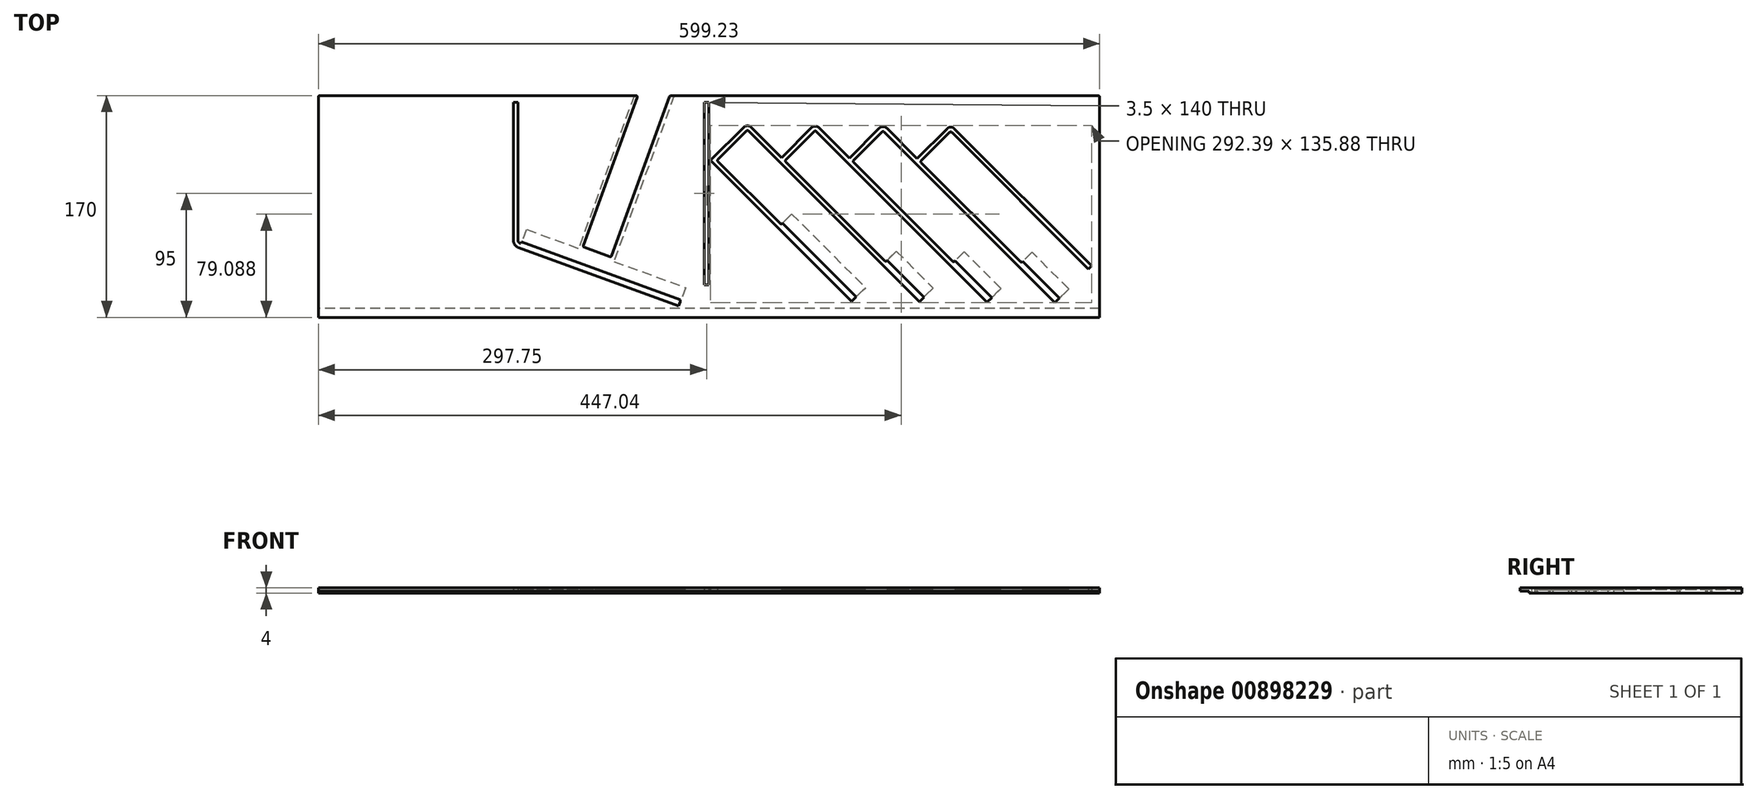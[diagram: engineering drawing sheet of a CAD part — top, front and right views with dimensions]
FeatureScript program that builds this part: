
annotation { "Feature Type Name" : "Feature", "Feature Type Description" : "" }
export const myFeature = defineFeature(function(context is Context, id is Id, definition is map)
    precondition{}
    {
        {
            var Q0;
            Q0=qCreatedBy(makeId("Top.planeOp"),FACE);
            var sketch = newSketch(context, id + "F0", { "sketchPlane" : qUnion([Q0])});
            skLineSegment(sketch, "E0.left", {"start": v(299.43, -88.5) * mm, "end": v(299.43, 80.5) * mm});
            skLineSegment(sketch, "E0.right", {"start": v(-299.8, -88.5) * mm, "end": v(-299.8, 80.5) * mm});
            skPoint(sketch, "E0.middle", {"position": v(0, 0) * mm});
            skLineSegment(sketch, "E1", {"start": v(188.08, 56.3) * mm, "end": v(293.43, -49.07) * mm});
            skLineSegment(sketch, "E2", {"start": v(293.43, -49.07) * mm, "end": v(290.96, -51.54) * mm});
            skLineSegment(sketch, "E3", {"start": v(265.15, -77.35) * mm, "end": v(156.96, 30.84) * mm});
            skLineSegment(sketch, "E4", {"start": v(159.44, 33.31) * mm, "end": v(182.42, 56.3) * mm});
            skLineSegment(sketch, "E5", {"start": v(238.63, -45.88) * mm, "end": v(162.62, 30.13) * mm});
            skLineSegment(sketch, "E6", {"start": v(162.62, 31.54) * mm, "end": v(184.54, 53.46) * mm});
            skLineSegment(sketch, "E7", {"start": v(185.95, 53.46) * mm, "end": v(290.96, -51.54) * mm});
            skLineSegment(sketch, "E8.trimOffspring", {"start": v(267.62, -74.88) * mm, "end": v(265.15, -77.35) * mm});
            skLineSegment(sketch, "E9", {"start": v(136.1, 56.65) * mm, "end": v(159.44, 33.31) * mm});
            skLineSegment(sketch, "E10", {"start": v(213.18, -77) * mm, "end": v(105, 31.2) * mm});
            skLineSegment(sketch, "E11", {"start": v(107.47, 33.67) * mm, "end": v(130.45, 56.65) * mm});
            skLineSegment(sketch, "E12", {"start": v(186.66, -45.53) * mm, "end": v(110.65, 30.48) * mm});
            skLineSegment(sketch, "E13", {"start": v(110.65, 31.9) * mm, "end": v(132.57, 53.82) * mm});
            skLineSegment(sketch, "E14", {"start": v(133.98, 53.82) * mm, "end": v(156.96, 30.84) * mm});
            skLineSegment(sketch, "E15.trimOffspring", {"start": v(215.65, -74.52) * mm, "end": v(213.18, -77) * mm});
            skLineSegment(sketch, "E16", {"start": v(84.13, 57) * mm, "end": v(107.47, 33.67) * mm});
            skLineSegment(sketch, "E17", {"start": v(161.2, -76.64) * mm, "end": v(53.02, 31.54) * mm});
            skLineSegment(sketch, "E18", {"start": v(55.5, 34.02) * mm, "end": v(78.47, 57) * mm});
            skLineSegment(sketch, "E19", {"start": v(134.69, -45.18) * mm, "end": v(58.67, 30.84) * mm});
            skLineSegment(sketch, "E20", {"start": v(58.67, 32.25) * mm, "end": v(80.6, 54.17) * mm});
            skLineSegment(sketch, "E21", {"start": v(82, 54.17) * mm, "end": v(105, 31.2) * mm});
            skLineSegment(sketch, "E22.trimOffspring", {"start": v(163.68, -74.17) * mm, "end": v(161.2, -76.64) * mm});
            skLineSegment(sketch, "E23", {"start": v(32.16, 57.35) * mm, "end": v(55.5, 34.02) * mm});
            skLineSegment(sketch, "E24", {"start": v(109.23, -76.29) * mm, "end": v(1.05, 31.9) * mm});
            skLineSegment(sketch, "E25", {"start": v(1.05, 31.9) * mm, "end": v(26.5, 57.35) * mm});
            skLineSegment(sketch, "E26", {"start": v(54.43, -16.54) * mm, "end": v(6.7, 31.2) * mm});
            skLineSegment(sketch, "E27", {"start": v(6.7, 32.6) * mm, "end": v(28.62, 54.53) * mm});
            skLineSegment(sketch, "E28", {"start": v(30.04, 54.53) * mm, "end": v(53.02, 31.54) * mm});
            skLineSegment(sketch, "E29.trimOffspring", {"start": v(111.7, -73.81) * mm, "end": v(109.23, -76.29) * mm});
            skLineSegment(sketch, "E30", {"start": v(-3.8, 76.5) * mm, "end": v(-3.8, -63.5) * mm});
            skLineSegment(sketch, "E31", {"start": v(-3.8, -63.5) * mm, "end": v(-0.3, -63.5) * mm});
            skLineSegment(sketch, "E32", {"start": v(-0.3, -63.5) * mm, "end": v(-0.3, 76.5) * mm});
            skLineSegment(sketch, "E33", {"start": v(-0.3, 76.5) * mm, "end": v(-3.8, 76.5) * mm});
            skLineSegment(sketch, "E34", {"start": v(-299.8, -88.5) * mm, "end": v(299.43, -88.5) * mm});
            skLineSegment(sketch, "E35", {"start": v(-150.3, 76.5) * mm, "end": v(-150.3, -29.3) * mm});
            skLineSegment(sketch, "E36", {"start": v(-146.36, -34.93) * mm, "end": v(-23.49, -79.8) * mm});
            skLineSegment(sketch, "E37", {"start": v(-23.49, -79.8) * mm, "end": v(-22.29, -76.5) * mm});
            skLineSegment(sketch, "E38", {"start": v(-146.8, -29.09) * mm, "end": v(-146.8, 76.5) * mm});
            skPoint(sketch, "E39.orphan", {"position": v(-299.8, -121.5) * mm});
            skPoint(sketch, "E40.orphan", {"position": v(299.43, -122.07) * mm});
            skPoint(sketch, "E41.visualSharp", {"position": v(-146.8, -31.19) * mm});
            skArc(sketch, "E41.filletArc", {"start": v(-146.8, -29.09) * mm, "mid": v(-146.26, -30.8) * mm, "end": v(-144.83, -31.9) * mm});
            skPoint(sketch, "E42.visualSharp", {"position": v(-150.3, -33.5) * mm});
            skArc(sketch, "E42.filletArc", {"start": v(-150.3, -29.3) * mm, "mid": v(-149.22, -32.74) * mm, "end": v(-146.36, -34.93) * mm});
            skLineSegment(sketch, "E43", {"start": v(267.62, -74.88) * mm, "end": v(268.69, -73.81) * mm});
            skLineSegment(sketch, "E44", {"start": v(268.69, -73.81) * mm, "end": v(240.4, -45.53) * mm});
            skLineSegment(sketch, "E45", {"start": v(240.4, -45.53) * mm, "end": v(240.05, -45.88) * mm});
            skLineSegment(sketch, "E46", {"start": v(215.65, -74.52) * mm, "end": v(216.71, -73.46) * mm});
            skLineSegment(sketch, "E47", {"start": v(216.71, -73.46) * mm, "end": v(188.43, -45.18) * mm});
            skLineSegment(sketch, "E48", {"start": v(188.43, -45.18) * mm, "end": v(188.08, -45.53) * mm});
            skLineSegment(sketch, "E49", {"start": v(163.68, -74.17) * mm, "end": v(164.74, -73.1) * mm});
            skLineSegment(sketch, "E50", {"start": v(164.74, -73.1) * mm, "end": v(136.46, -44.82) * mm});
            skLineSegment(sketch, "E51", {"start": v(136.46, -44.82) * mm, "end": v(136.1, -45.18) * mm});
            skLineSegment(sketch, "E52", {"start": v(111.7, -73.81) * mm, "end": v(112.77, -72.75) * mm});
            skLineSegment(sketch, "E53", {"start": v(112.77, -72.75) * mm, "end": v(56.2, -16.19) * mm});
            skLineSegment(sketch, "E54", {"start": v(56.2, -16.19) * mm, "end": v(55.85, -16.54) * mm});
            skLineSegment(sketch, "E55", {"start": v(-144.83, -31.9) * mm, "end": v(-144.31, -30.5) * mm});
            skLineSegment(sketch, "E56", {"start": v(-144.31, -30.5) * mm, "end": v(-101.09, -46.23) * mm});
            skPoint(sketch, "E57.visualSharp", {"position": v(29.33, 60.18) * mm});
            skArc(sketch, "E57.filletArc", {"start": v(32.16, 57.35) * mm, "mid": v(29.33, 58.53) * mm, "end": v(26.5, 57.35) * mm});
            skPoint(sketch, "E58.visualSharp", {"position": v(81.3, 59.83) * mm});
            skArc(sketch, "E58.filletArc", {"start": v(84.13, 57) * mm, "mid": v(81.3, 58.17) * mm, "end": v(78.47, 57) * mm});
            skPoint(sketch, "E59.visualSharp", {"position": v(133.27, 59.48) * mm});
            skArc(sketch, "E59.filletArc", {"start": v(136.1, 56.65) * mm, "mid": v(133.27, 57.82) * mm, "end": v(130.45, 56.65) * mm});
            skPoint(sketch, "E60.visualSharp", {"position": v(185.25, 59.12) * mm});
            skArc(sketch, "E60.filletArc", {"start": v(188.08, 56.3) * mm, "mid": v(185.25, 57.46) * mm, "end": v(182.42, 56.3) * mm});
            skPoint(sketch, "E61.visualSharp", {"position": v(6, 31.9) * mm});
            skArc(sketch, "E61.filletArc", {"start": v(6.7, 32.6) * mm, "mid": v(6.4, 31.9) * mm, "end": v(6.7, 31.2) * mm});
            skPoint(sketch, "E62.visualSharp", {"position": v(57.97, 31.54) * mm});
            skArc(sketch, "E62.filletArc", {"start": v(58.67, 32.25) * mm, "mid": v(58.38, 31.54) * mm, "end": v(58.67, 30.84) * mm});
            skPoint(sketch, "E63.visualSharp", {"position": v(109.94, 31.2) * mm});
            skArc(sketch, "E63.filletArc", {"start": v(110.65, 31.9) * mm, "mid": v(110.35, 31.2) * mm, "end": v(110.65, 30.48) * mm});
            skPoint(sketch, "E64.visualSharp", {"position": v(161.91, 30.84) * mm});
            skArc(sketch, "E64.filletArc", {"start": v(162.62, 31.54) * mm, "mid": v(162.33, 30.84) * mm, "end": v(162.62, 30.13) * mm});
            skPoint(sketch, "E65.visualSharp", {"position": v(81.3, 54.88) * mm});
            skArc(sketch, "E65.filletArc", {"start": v(82, 54.17) * mm, "mid": v(81.3, 54.46) * mm, "end": v(80.6, 54.17) * mm});
            skPoint(sketch, "E66.visualSharp", {"position": v(29.33, 55.23) * mm});
            skArc(sketch, "E66.filletArc", {"start": v(30.04, 54.53) * mm, "mid": v(29.33, 54.82) * mm, "end": v(28.62, 54.53) * mm});
            skPoint(sketch, "E67.visualSharp", {"position": v(133.27, 54.53) * mm});
            skArc(sketch, "E67.filletArc", {"start": v(133.98, 53.82) * mm, "mid": v(133.27, 54.11) * mm, "end": v(132.57, 53.82) * mm});
            skPoint(sketch, "E68.visualSharp", {"position": v(185.25, 54.17) * mm});
            skArc(sketch, "E68.filletArc", {"start": v(185.95, 53.46) * mm, "mid": v(185.25, 53.76) * mm, "end": v(184.54, 53.46) * mm});
            skLineSegment(sketch, "E69", {"start": v(-96.58, -33.5) * mm, "end": v(-55.2, 80.16) * mm});
            skLineSegment(sketch, "E70", {"start": v(-32.58, 75.09) * mm, "end": v(-74.96, -41.37) * mm});
            skLineSegment(sketch, "E71", {"start": v(-76.25, -41.97) * mm, "end": v(-95.98, -34.79) * mm});
            skLineSegment(sketch, "E72", {"start": v(-298.8, 81.5) * mm, "end": v(-202.52, 81.5) * mm});
            skLineSegment(sketch, "E73", {"start": v(-150.3, 76.5) * mm, "end": v(-146.8, 76.5) * mm});
            skLineSegment(sketch, "E74", {"start": v(-32.58, 75.09) * mm, "end": v(-30.48, 80.84) * mm});
            skLineSegment(sketch, "E75.trimOffspring", {"start": v(-175.92, 81.5) * mm, "end": v(-56.15, 81.5) * mm});
            skLineSegment(sketch, "E76.trimOffspring", {"start": v(-29.54, 81.5) * mm, "end": v(298.43, 81.5) * mm});
            skPoint(sketch, "E77.visualSharp", {"position": v(-299.8, 81.5) * mm});
            skArc(sketch, "E77.filletArc", {"start": v(-298.8, 81.5) * mm, "mid": v(-299.5, 81.2) * mm, "end": v(-299.8, 80.5) * mm});
            skPoint(sketch, "E78.visualSharp", {"position": v(299.43, 81.5) * mm});
            skArc(sketch, "E78.filletArc", {"start": v(299.43, 80.5) * mm, "mid": v(299.14, 81.2) * mm, "end": v(298.43, 81.5) * mm});
            skPoint(sketch, "E79.visualSharp", {"position": v(-30.24, 81.5) * mm});
            skArc(sketch, "E79.filletArc", {"start": v(-29.54, 81.5) * mm, "mid": v(-30.12, 81.32) * mm, "end": v(-30.48, 80.84) * mm});
            skPoint(sketch, "E80.visualSharp", {"position": v(-54.72, 81.5) * mm});
            skArc(sketch, "E80.filletArc", {"start": v(-55.2, 80.16) * mm, "mid": v(-55.33, 81.07) * mm, "end": v(-56.15, 81.5) * mm});
            skPoint(sketch, "E81.visualSharp", {"position": v(-101.6, -47.64) * mm});
            skLineSegment(sketch, "E82", {"start": v(-202.52, 81.5) * mm, "end": v(-175.92, 81.5) * mm});
            skLineSegment(sketch, "E83", {"start": v(-101.09, -46.23) * mm, "end": v(-69.14, -57.86) * mm});
            skPoint(sketch, "E84.visualSharp", {"position": v(-96.92, -34.45) * mm});
            skArc(sketch, "E84.filletArc", {"start": v(-96.58, -33.5) * mm, "mid": v(-96.54, -34.27) * mm, "end": v(-95.98, -34.79) * mm});
            skPoint(sketch, "E85.visualSharp", {"position": v(-75.3, -42.31) * mm});
            skArc(sketch, "E85.filletArc", {"start": v(-76.25, -41.97) * mm, "mid": v(-75.48, -41.94) * mm, "end": v(-74.96, -41.37) * mm});
            skPoint(sketch, "E86.visualSharp", {"position": v(-69.65, -59.27) * mm});
            skPoint(sketch, "E87.visualSharp", {"position": v(55.14, -17.25) * mm});
            skArc(sketch, "E87.filletArc", {"start": v(54.43, -16.54) * mm, "mid": v(55.14, -16.83) * mm, "end": v(55.85, -16.54) * mm});
            skPoint(sketch, "E88.visualSharp", {"position": v(135.4, -45.88) * mm});
            skArc(sketch, "E88.filletArc", {"start": v(134.69, -45.18) * mm, "mid": v(135.4, -45.47) * mm, "end": v(136.1, -45.18) * mm});
            skPoint(sketch, "E89.visualSharp", {"position": v(187.37, -46.24) * mm});
            skArc(sketch, "E89.filletArc", {"start": v(186.66, -45.53) * mm, "mid": v(187.37, -45.82) * mm, "end": v(188.08, -45.53) * mm});
            skPoint(sketch, "E90.visualSharp", {"position": v(239.34, -46.6) * mm});
            skArc(sketch, "E90.filletArc", {"start": v(238.63, -45.88) * mm, "mid": v(239.34, -46.18) * mm, "end": v(240.05, -45.88) * mm});
            skLineSegment(sketch, "E91", {"start": v(-69.14, -57.86) * mm, "end": v(-22.29, -74.91) * mm});
            skLineSegment(sketch, "E92", {"start": v(-22.29, -74.91) * mm, "end": v(-22.29, -76.5) * mm});
            skSolve(sketch);
        }
        {
            var Q0;
            Q0=qSketchRegion(id+"F0",true);
            extrude(context, id + "F1", {"entities" : qUnion([Q0]), "depth" : 4 * mm});
        }
        {
            var Q0;
            Q0=makeQuery(id+"F1.opExtrude","CAP_FACE",FACE,{"disambiguationData":[OSD([sQuery(id+"F0.wireOp",EDGE,"E0.top"),sQuery(id+"F0.wireOp",EDGE,"E0.left"),sQuery(id+"F0.wireOp",EDGE,"E0.right"),sQuery(id+"F0.wireOp",EDGE,"E1"),sQuery(id+"F0.wireOp",EDGE,"E2"),sQuery(id+"F0.wireOp",EDGE,"E3"),sQuery(id+"F0.wireOp",EDGE,"E4"),sQuery(id+"F0.wireOp",EDGE,"E5"),sQuery(id+"F0.wireOp",EDGE,"E6"),sQuery(id+"F0.wireOp",EDGE,"E7"),sQuery(id+"F0.wireOp",EDGE,"E8.trimOffspring"),sQuery(id+"F0.wireOp",EDGE,"E9"),sQuery(id+"F0.wireOp",EDGE,"E10"),sQuery(id+"F0.wireOp",EDGE,"E11"),sQuery(id+"F0.wireOp",EDGE,"E12"),sQuery(id+"F0.wireOp",EDGE,"E13"),sQuery(id+"F0.wireOp",EDGE,"E14"),sQuery(id+"F0.wireOp",EDGE,"E15.trimOffspring"),sQuery(id+"F0.wireOp",EDGE,"E16"),sQuery(id+"F0.wireOp",EDGE,"E17"),sQuery(id+"F0.wireOp",EDGE,"E18"),sQuery(id+"F0.wireOp",EDGE,"E19"),sQuery(id+"F0.wireOp",EDGE,"E20"),sQuery(id+"F0.wireOp",EDGE,"E21"),sQuery(id+"F0.wireOp",EDGE,"E22.trimOffspring"),sQuery(id+"F0.wireOp",EDGE,"E23"),sQuery(id+"F0.wireOp",EDGE,"E24"),sQuery(id+"F0.wireOp",EDGE,"E25"),sQuery(id+"F0.wireOp",EDGE,"E26"),sQuery(id+"F0.wireOp",EDGE,"E27"),sQuery(id+"F0.wireOp",EDGE,"E28"),sQuery(id+"F0.wireOp",EDGE,"E29.trimOffspring"),sQuery(id+"F0.wireOp",EDGE,"E30"),sQuery(id+"F0.wireOp",EDGE,"E31"),sQuery(id+"F0.wireOp",EDGE,"E32"),sQuery(id+"F0.wireOp",EDGE,"E33"),sQuery(id+"F0.wireOp",EDGE,"E34"),sQuery(id+"F0.wireOp",EDGE,"8IGRu6me-QNIK-KxZd-YoE2-obK5ITrom9I0"),sQuery(id+"F0.wireOp",EDGE,"ET2SPLNs-E16K-yzbb-k3nE-j9QhBZggRVGa"),sQuery(id+"F0.wireOp",EDGE,"ztZXadrO-MKuG-NGwv-NWga-JcB19pq0CV4f"),sQuery(id+"F0.wireOp",EDGE,"rMW3URec-0C8R-i97H-GSKa-9mzG0eoT4OPy"),sQuery(id+"F0.wireOp",EDGE,"l2nM3VSt-hcp3-IfvZ-Vc9z-1xBHJXzoDHYJ"),sQuery(id+"F0.wireOp",EDGE,"7f4JG1PR-e8fq-IrSw-QAHP-AJHShleLprlO"),sQuery(id+"F0.wireOp",EDGE,"E35"),sQuery(id+"F0.wireOp",EDGE,"E36"),sQuery(id+"F0.wireOp",EDGE,"E37"),sQuery(id+"F0.wireOp",EDGE,"Wq4ZA5YM-xzJ0-yVii-3j4H-AYTGBk09bdcb"),sQuery(id+"F0.wireOp",EDGE,"E38"),sQuery(id+"F0.wireOp",EDGE,"gIA7jmsT-nlDV-00d0-acZ5-NCJ1QFAXyANS")])],"isStart":true});
            var sketch = newSketch(context, id + "F2", { "sketchPlane" : qUnion([Q0])});
            skLineSegment(sketch, "E93", {"start": v(-299.8, 88.5) * mm, "end": v(299.43, 88.5) * mm});
            skLineSegment(sketch, "E94", {"start": v(299.43, 88.5) * mm, "end": v(299.43, 81.5) * mm});
            skLineSegment(sketch, "E95", {"start": v(299.43, 81.5) * mm, "end": v(-299.8, 81.5) * mm});
            skLineSegment(sketch, "E96", {"start": v(-299.8, 81.5) * mm, "end": v(-299.8, 88.5) * mm});
            skLineSegment(sketch, "E97", {"start": v(268.69, 73.81) * mm, "end": v(275.76, 66.74) * mm});
            skLineSegment(sketch, "E98", {"start": v(275.76, 66.74) * mm, "end": v(247.47, 38.46) * mm});
            skLineSegment(sketch, "E99", {"start": v(247.47, 38.46) * mm, "end": v(240.4, 45.53) * mm});
            skLineSegment(sketch, "E100", {"start": v(216.71, 73.46) * mm, "end": v(223.78, 66.39) * mm});
            skLineSegment(sketch, "E101", {"start": v(223.78, 66.39) * mm, "end": v(195.5, 38.1) * mm});
            skLineSegment(sketch, "E102", {"start": v(195.5, 38.1) * mm, "end": v(188.43, 45.18) * mm});
            skLineSegment(sketch, "E103", {"start": v(268.69, 73.81) * mm, "end": v(240.4, 45.53) * mm});
            skLineSegment(sketch, "E104", {"start": v(216.71, 73.46) * mm, "end": v(188.43, 45.18) * mm});
            skLineSegment(sketch, "E105", {"start": v(164.74, 73.1) * mm, "end": v(136.46, 44.82) * mm});
            skLineSegment(sketch, "E106", {"start": v(136.46, 44.82) * mm, "end": v(143.53, 37.75) * mm});
            skLineSegment(sketch, "E107", {"start": v(143.53, 37.75) * mm, "end": v(171.81, 66.04) * mm});
            skLineSegment(sketch, "E108", {"start": v(171.81, 66.04) * mm, "end": v(164.74, 73.1) * mm});
            skLineSegment(sketch, "E109", {"start": v(112.77, 72.75) * mm, "end": v(56.2, 16.19) * mm});
            skLineSegment(sketch, "E110", {"start": v(56.2, 16.19) * mm, "end": v(63.27, 9.11) * mm});
            skLineSegment(sketch, "E111", {"start": v(63.27, 9.11) * mm, "end": v(119.84, 65.68) * mm});
            skLineSegment(sketch, "E112", {"start": v(119.84, 65.68) * mm, "end": v(112.77, 72.75) * mm});
            skLineSegment(sketch, "E113", {"start": v(-1004.52, -17.26) * mm, "end": v(-1004.52, -17.26) * mm});
            skLineSegment(sketch, "E114", {"start": v(-52.4, -86.26) * mm, "end": v(-55.41, -87.35) * mm});
            skLineSegment(sketch, "E115", {"start": v(-55.41, -87.35) * mm, "end": v(-100.24, 35.8) * mm});
            skLineSegment(sketch, "E116", {"start": v(-100.24, 35.8) * mm, "end": v(-140.4, 21.19) * mm});
            skLineSegment(sketch, "E117", {"start": v(-140.4, 21.19) * mm, "end": v(-143.98, 31.05) * mm});
            skLineSegment(sketch, "E118", {"start": v(-28.6, -86.07) * mm, "end": v(-25.59, -84.97) * mm});
            skLineSegment(sketch, "E119", {"start": v(-25.59, -84.97) * mm, "end": v(-73.14, 45.67) * mm});
            skLineSegment(sketch, "E120", {"start": v(-52.4, -86.26) * mm, "end": v(-96, 33.37) * mm});
            skLineSegment(sketch, "E121", {"start": v(-96, 33.37) * mm, "end": v(-75.15, 41.3) * mm});
            skLineSegment(sketch, "E122", {"start": v(-143.98, 31.05) * mm, "end": v(-21.7, 75.56) * mm});
            skLineSegment(sketch, "E123", {"start": v(-73.14, 45.67) * mm, "end": v(-18.14, 65.68) * mm});
            skLineSegment(sketch, "E124", {"start": v(-18.14, 65.68) * mm, "end": v(-21.7, 75.56) * mm});
            skLineSegment(sketch, "E125", {"start": v(-75.15, 41.3) * mm, "end": v(-28.77, -86.14) * mm});
            skLineSegment(sketch, "E126", {"start": v(-28.77, -86.14) * mm, "end": v(-28.6, -86.07) * mm});
            skSolve(sketch);
        }
        {
            var Q0;
            Q0=makeQuery(id+"F2.imprint","IMPRINT",FACE,{"disambiguationData":[TD([[makeQuery(id+"F2.imprint","IMPRINT",EDGE,{"derivedFrom":sQuery(id+"F2.wireOp",EDGE,"E97")}),-1.0]])]});
            var Q1;
            Q1=makeQuery(id+"F2.imprint","IMPRINT",FACE,{"disambiguationData":[TD([[makeQuery(id+"F2.imprint","IMPRINT",EDGE,{"derivedFrom":sQuery(id+"F2.wireOp",EDGE,"E100")}),-1.0]])]});
            var Q2;
            Q2=makeQuery(id+"F2.imprint","IMPRINT",FACE,{"disambiguationData":[TD([[makeQuery(id+"F2.imprint","IMPRINT",EDGE,{"derivedFrom":sQuery(id+"F2.wireOp",EDGE,"E105")}),1.0]])]});
            var Q3;
            Q3=makeQuery(id+"F2.imprint","IMPRINT",FACE,{"disambiguationData":[TD([[makeQuery(id+"F2.imprint","IMPRINT",EDGE,{"derivedFrom":sQuery(id+"F2.wireOp",EDGE,"E109")}),1.0]])]});
            var Q4;
            {var subQ1=sQuery(id+"F2.wireOp",EDGE,"8fb6a346-390b-43d0-a156-07e60583d9f8");Q4=makeQuery(id+"F2.imprint","IMPRINT",FACE,{"disambiguationData":[TD([[makeQuery(id+"F2.imprint","IMPRINT",EDGE,{"derivedFrom":subQ1}),1.0]])]});}
            var Q5;
            {var subQ0=sQuery(id+"F2.wireOp",EDGE,"E114");Q5=makeQuery(id+"F2.imprint","IMPRINT",FACE,{"disambiguationData":[TD([[makeQuery(id+"F2.imprint","IMPRINT",EDGE,{"derivedFrom":subQ0}),-1.0]])]});}
            var Q6;
            {var subQ0=sQuery(id+"F2.wireOp",EDGE,"E118");Q6=makeQuery(id+"F2.imprint","IMPRINT",FACE,{"disambiguationData":[TD([[makeQuery(id+"F2.imprint","IMPRINT",EDGE,{"derivedFrom":subQ0}),1.0]])]});}
            var Q7;
            {var subQ6=sQuery(id+"F2.wireOp",EDGE,"a6810e08-8d53-41db-9dac-b19748a4023a");Q7=makeQuery(id+"F2.imprint","IMPRINT",FACE,{"disambiguationData":[TD([[makeQuery(id+"F2.imprint","IMPRINT",EDGE,{"derivedFrom":subQ6}),-1.0]])]});}
            var Q8;
            {var subQ1=sQuery(id+"F2.wireOp",EDGE,"E116");Q8=makeQuery(id+"F2.imprint","IMPRINT",FACE,{"disambiguationData":[TD([[makeQuery(id+"F2.imprint","IMPRINT",EDGE,{"derivedFrom":subQ1}),-1.0]])]});}
            var Q9;
            {var subQ8=sQuery(id+"F2.wireOp",EDGE,"5a9c356d-3bd6-4c7f-bf7b-0702d958a0c5");Q9=makeQuery(id+"F2.imprint","IMPRINT",FACE,{"disambiguationData":[TD([[makeQuery(id+"F2.imprint","IMPRINT",EDGE,{"derivedFrom":subQ8}),-1.0]])]});}
            extrude(context, id + "F3", {"entities" : qUnion([Q0, Q1, Q2, Q3, Q4, Q5, Q6, Q7, Q8, Q9]), "operationType" : NewBodyOperationType.REMOVE, "oppositeDirection" : true, "depth" : 2.5 * mm});
        }
        {
            var Q0;
            Q0=makeQuery(id+"F2.imprint","IMPRINT",FACE,{"disambiguationData":[TD([[makeQuery(id+"F2.imprint","IMPRINT",EDGE,{"derivedFrom":sQuery(id+"F2.wireOp",EDGE,"E93")}),-1.0]])]});
            extrude(context, id + "F4", {"entities" : qUnion([Q0]), "operationType" : NewBodyOperationType.REMOVE, "oppositeDirection" : true, "depth" : 1.5 * mm});
        }
    });
